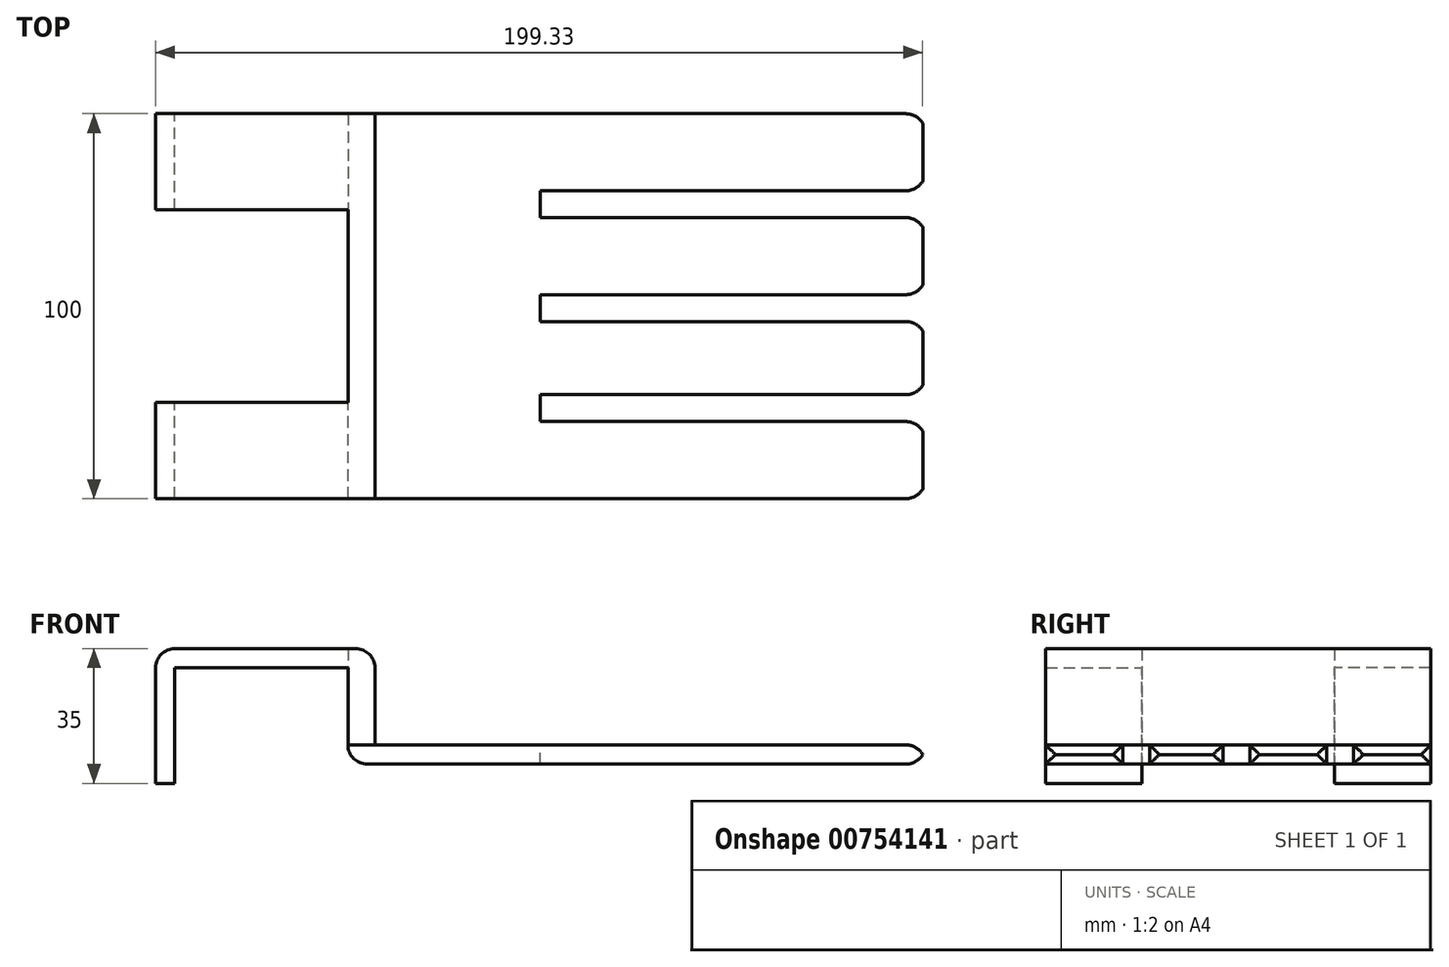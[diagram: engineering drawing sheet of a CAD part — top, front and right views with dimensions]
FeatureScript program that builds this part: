
annotation { "Feature Type Name" : "Feature", "Feature Type Description" : "" }
export const myFeature = defineFeature(function(context is Context, id is Id, definition is map)
    precondition{}
    {
        {
            var Q0;
            Q0=qCreatedBy(makeId("Top.planeOp"),FACE);
            var sketch = newSketch(context, id + "F0", { "sketchPlane" : qUnion([Q0])});
            skLineSegment(sketch, "E0.bottom", {"start": v(-77.43, 52.19) * mm, "end": v(72.57, 52.19) * mm});
            skLineSegment(sketch, "E0.top", {"start": v(-77.43, -47.81) * mm, "end": v(72.57, -47.81) * mm});
            skLineSegment(sketch, "E0.left", {"start": v(-77.43, 52.19) * mm, "end": v(-77.43, -47.81) * mm});
            skLineSegment(sketch, "E0.right", {"start": v(72.57, 52.19) * mm, "end": v(72.57, -47.81) * mm});
            skSolve(sketch);
        }
        {
            var Q0;
            Q0=makeQuery(id+"F0.imprint","IMPRINT",FACE,{"disambiguationData":[TD([[makeQuery(id+"F0.imprint","IMPRINT",EDGE,{"derivedFrom":sQuery(id+"F0.wireOp",EDGE,"E0.bottom")}),-1.0]])]});
            extrude(context, id + "F1", {"entities" : qUnion([Q0]), "depth" : 5 * mm, "offsetDistance" : 25 * mm});
        }
        {
            var Q0;
            Q0=makeQuery(id+"F1.opExtrude","CAP_FACE",FACE,{"disambiguationData":[OSD([sQuery(id+"F0.wireOp",EDGE,"E0.bottom"),sQuery(id+"F0.wireOp",EDGE,"E0.top"),sQuery(id+"F0.wireOp",EDGE,"E0.left"),sQuery(id+"F0.wireOp",EDGE,"E0.right")])],"isStart":false});
            var sketch = newSketch(context, id + "F2", { "sketchPlane" : qUnion([Q0])});
            skLineSegment(sketch, "E1", {"start": v(-27.43, 52.19) * mm, "end": v(-27.43, -47.81) * mm, "construction": true});
            skLineSegment(sketch, "E2.bottom", {"start": v(-27.43, 32.19) * mm, "end": v(72.57, 32.19) * mm});
            skLineSegment(sketch, "E2.top", {"start": v(-27.43, 25.19) * mm, "end": v(72.57, 25.19) * mm});
            skLineSegment(sketch, "E2.left", {"start": v(-27.43, 32.19) * mm, "end": v(-27.43, 25.19) * mm});
            skLineSegment(sketch, "E2.right", {"start": v(72.57, 32.19) * mm, "end": v(72.57, 25.19) * mm});
            skLineSegment(sketch, "E3.bottom", {"start": v(-27.43, -20.81) * mm, "end": v(72.57, -20.81) * mm});
            skLineSegment(sketch, "E3.top", {"start": v(-27.43, -27.81) * mm, "end": v(72.57, -27.81) * mm});
            skLineSegment(sketch, "E3.left", {"start": v(-27.43, -20.81) * mm, "end": v(-27.43, -27.81) * mm});
            skLineSegment(sketch, "E3.right", {"start": v(72.57, -20.81) * mm, "end": v(72.57, -27.81) * mm});
            skLineSegment(sketch, "E4.bottom", {"start": v(-27.43, 5.19) * mm, "end": v(72.57, 5.19) * mm});
            skLineSegment(sketch, "E4.top", {"start": v(-27.43, -1.81) * mm, "end": v(72.57, -1.81) * mm});
            skLineSegment(sketch, "E4.left", {"start": v(-27.43, 5.19) * mm, "end": v(-27.43, -1.81) * mm});
            skLineSegment(sketch, "E4.right", {"start": v(72.57, 5.19) * mm, "end": v(72.57, -1.81) * mm});
            skSolve(sketch);
        }
        {
            var Q0;
            Q0=makeQuery(id+"F2.imprint","IMPRINT",FACE,{"disambiguationData":[TD([[makeQuery(id+"F2.imprint","IMPRINT",EDGE,{"derivedFrom":sQuery(id+"F2.wireOp",EDGE,"E2.bottom")}),-1.0]])]});
            var Q1;
            Q1=makeQuery(id+"F2.imprint","IMPRINT",FACE,{"disambiguationData":[TD([[makeQuery(id+"F2.imprint","IMPRINT",EDGE,{"derivedFrom":sQuery(id+"F2.wireOp",EDGE,"E4.bottom")}),-1.0]])]});
            var Q2;
            Q2=makeQuery(id+"F2.imprint","IMPRINT",FACE,{"disambiguationData":[TD([[makeQuery(id+"F2.imprint","IMPRINT",EDGE,{"derivedFrom":sQuery(id+"F2.wireOp",EDGE,"E3.bottom")}),-1.0]])]});
            extrude(context, id + "F3", {"entities" : qUnion([Q0, Q1, Q2]), "operationType" : NewBodyOperationType.REMOVE, "endBound" : BoundingType.THROUGH_ALL, "oppositeDirection" : true, "depth" : 25 * mm, "offsetDistance" : 25 * mm});
        }
        {
            var Q0;
            Q0=makeQuery(id+"F1.opExtrude","CAP_FACE",FACE,{"disambiguationData":[OSD([sQuery(id+"F0.wireOp",EDGE,"E0.bottom"),sQuery(id+"F0.wireOp",EDGE,"E0.top"),sQuery(id+"F0.wireOp",EDGE,"E0.left"),sQuery(id+"F0.wireOp",EDGE,"E0.right")])],"isStart":false});
            var sketch = newSketch(context, id + "F4", { "sketchPlane" : qUnion([Q0])});
            skLineSegment(sketch, "E5.bottom", {"start": v(-77.43, 52.19) * mm, "end": v(-70.43, 52.19) * mm});
            skLineSegment(sketch, "E5.top", {"start": v(-77.43, -47.81) * mm, "end": v(-70.43, -47.81) * mm});
            skLineSegment(sketch, "E5.left", {"start": v(-77.43, 52.19) * mm, "end": v(-77.43, -47.81) * mm});
            skLineSegment(sketch, "E5.right", {"start": v(-70.43, 52.19) * mm, "end": v(-70.43, -47.81) * mm});
            skSolve(sketch);
        }
        {
            var Q0;
            Q0=makeQuery(id+"F4.imprint","IMPRINT",FACE,{"disambiguationData":[TD([[makeQuery(id+"F4.imprint","IMPRINT",EDGE,{"derivedFrom":sQuery(id+"F4.wireOp",EDGE,"E5.bottom")}),-1.0]])]});
            extrude(context, id + "F5", {"entities" : qUnion([Q0]), "depth" : 25 * mm, "offsetDistance" : 25 * mm});
        }
        {
            var Q0;
            Q0=makeQuery(id+"F5.opExtrude","SWEPT_FACE",FACE,{"disambiguationData":[OSD([sQuery(id+"F4.wireOp",EDGE,"E5.left")])]});
            var sketch = newSketch(context, id + "F6", { "sketchPlane" : qUnion([Q0])});
            skLineSegment(sketch, "E6.bottom", {"start": v(-52.19, 30) * mm, "end": v(-27.19, 30) * mm});
            skLineSegment(sketch, "E6.top", {"start": v(-52.19, 25) * mm, "end": v(-27.19, 25) * mm});
            skLineSegment(sketch, "E6.left", {"start": v(-52.19, 30) * mm, "end": v(-52.19, 25) * mm});
            skLineSegment(sketch, "E6.right", {"start": v(-27.19, 30) * mm, "end": v(-27.19, 25) * mm});
            skLineSegment(sketch, "E7.bottom", {"start": v(47.81, 30) * mm, "end": v(22.81, 30) * mm});
            skLineSegment(sketch, "E7.top", {"start": v(47.81, 25) * mm, "end": v(22.81, 25) * mm});
            skLineSegment(sketch, "E7.left", {"start": v(47.81, 30) * mm, "end": v(47.81, 25) * mm});
            skLineSegment(sketch, "E7.right", {"start": v(22.81, 30) * mm, "end": v(22.81, 25) * mm});
            skSolve(sketch);
        }
        {
            var Q0;
            Q0=makeQuery(id+"F6.imprint","IMPRINT",FACE,{"disambiguationData":[TD([[makeQuery(id+"F6.imprint","IMPRINT",EDGE,{"derivedFrom":sQuery(id+"F6.wireOp",EDGE,"E6.bottom")}),-1.0]])]});
            var Q1;
            Q1=makeQuery(id+"F6.imprint","IMPRINT",FACE,{"disambiguationData":[TD([[makeQuery(id+"F6.imprint","IMPRINT",EDGE,{"derivedFrom":sQuery(id+"F6.wireOp",EDGE,"E7.bottom")}),-1.0]])]});
            extrude(context, id + "F7", {"entities" : qUnion([Q0, Q1]), "operationType" : NewBodyOperationType.ADD, "depth" : 50 * mm, "offsetDistance" : 25 * mm});
        }
        {
            var Q0;
            Q0=makeQuery(id+"F7.opExtrude","SWEPT_FACE",FACE,{"disambiguationData":[OSD([sQuery(id+"F6.wireOp",EDGE,"E6.top")])]});
            var sketch = newSketch(context, id + "F8", { "sketchPlane" : qUnion([Q0])});
            skLineSegment(sketch, "E8.bottom", {"start": v(-127.43, -27.19) * mm, "end": v(-122.43, -27.19) * mm});
            skLineSegment(sketch, "E8.top", {"start": v(-127.43, -52.19) * mm, "end": v(-122.43, -52.19) * mm});
            skLineSegment(sketch, "E8.left", {"start": v(-127.43, -27.19) * mm, "end": v(-127.43, -52.19) * mm});
            skLineSegment(sketch, "E8.right", {"start": v(-122.43, -27.19) * mm, "end": v(-122.43, -52.19) * mm});
            skSolve(sketch);
        }
        {
            var Q0;
            Q0=makeQuery(id+"F7.opExtrude","SWEPT_FACE",FACE,{"disambiguationData":[OSD([sQuery(id+"F6.wireOp",EDGE,"E7.top")])]});
            var sketch = newSketch(context, id + "F9", { "sketchPlane" : qUnion([Q0])});
            skLineSegment(sketch, "E9.bottom", {"start": v(-127.43, 47.81) * mm, "end": v(-122.43, 47.81) * mm});
            skLineSegment(sketch, "E9.top", {"start": v(-127.43, 22.81) * mm, "end": v(-122.43, 22.81) * mm});
            skLineSegment(sketch, "E9.left", {"start": v(-127.43, 47.81) * mm, "end": v(-127.43, 22.81) * mm});
            skLineSegment(sketch, "E9.right", {"start": v(-122.43, 47.81) * mm, "end": v(-122.43, 22.81) * mm});
            skSolve(sketch);
        }
        {
            var Q0;
            Q0=makeQuery(id+"F9.imprint","IMPRINT",FACE,{"disambiguationData":[TD([[makeQuery(id+"F9.imprint","IMPRINT",EDGE,{"derivedFrom":sQuery(id+"F9.wireOp",EDGE,"E9.bottom")}),-1.0]])]});
            var Q1;
            Q1=makeQuery(id+"F8.imprint","IMPRINT",FACE,{"disambiguationData":[TD([[makeQuery(id+"F8.imprint","IMPRINT",EDGE,{"derivedFrom":sQuery(id+"F8.wireOp",EDGE,"E8.bottom")}),-1.0]])]});
            extrude(context, id + "F10", {"entities" : qUnion([Q0, Q1]), "operationType" : NewBodyOperationType.ADD, "depth" : 30 * mm, "offsetDistance" : 25 * mm});
        }
        {
            var Q0;
            Q0=makeQuery(id+"F7.opExtrude","CAP_EDGE",EDGE,{"disambiguationData":[OSD([sQuery(id+"F6.wireOp",EDGE,"E6.bottom")])],"isStart":false});
            var Q1;
            Q1=makeQuery(id+"F7.opExtrude","CAP_EDGE",EDGE,{"disambiguationData":[OSD([sQuery(id+"F6.wireOp",EDGE,"E7.bottom")])],"isStart":false});
            var Q2;
            Q2=makeQuery(id+"F5.opExtrude","CAP_EDGE",EDGE,{"disambiguationData":[OSD([sQuery(id+"F4.wireOp",EDGE,"E5.right")])],"isStart":false});
            var Q3;
            Q3=makeQuery(id+"F1.opExtrude","CAP_EDGE",EDGE,{"disambiguationData":[OSD([sQuery(id+"F0.wireOp",EDGE,"E0.left")])],"isStart":true});
            fillet(context, id + "F11", {"entities" : qUnion([Q0, Q1, Q2, Q3]), "radius" : 5 * mm, "tangentPropagation" : true, "allowEdgeOverflow" : false});
        }
        {
            var Q0;
            {var subQ0=sQuery(id+"F0.wireOp",EDGE,"E0.right");var subQ2=sQuery(id+"F0.wireOp",EDGE,"E0.top");Q0=makeQuery(id+"F3.boolean.opBoolean","SPLIT",FACE,{"disambiguationData":[TD([makeQuery(id+"F1.opExtrude","SWEPT_FACE",FACE,{"disambiguationData":[OSD([subQ2])]})])],"derivedFrom":makeQuery(id+"F1.opExtrude","SWEPT_FACE",FACE,{"disambiguationData":[OSD([subQ0])]})});}
            var Q1;
            {var subQ0=sQuery(id+"F0.wireOp",EDGE,"E0.right");Q1=makeQuery(id+"F3.boolean.opBoolean","SPLIT",FACE,{"disambiguationData":[TD([makeQuery(id+"F3.opExtrude","SWEPT_FACE",FACE,{"disambiguationData":[OSD([sQuery(id+"F2.wireOp",EDGE,"E3.bottom")])]})])],"derivedFrom":makeQuery(id+"F1.opExtrude","SWEPT_FACE",FACE,{"disambiguationData":[OSD([subQ0])]})});}
            var Q2;
            {var subQ0=sQuery(id+"F0.wireOp",EDGE,"E0.right");Q2=makeQuery(id+"F3.boolean.opBoolean","SPLIT",FACE,{"disambiguationData":[TD([makeQuery(id+"F3.opExtrude","SWEPT_FACE",FACE,{"disambiguationData":[OSD([sQuery(id+"F2.wireOp",EDGE,"E2.top")])]})])],"derivedFrom":makeQuery(id+"F1.opExtrude","SWEPT_FACE",FACE,{"disambiguationData":[OSD([subQ0])]})});}
            var Q3;
            {var subQ0=sQuery(id+"F0.wireOp",EDGE,"E0.bottom");var subQ1=sQuery(id+"F0.wireOp",EDGE,"E0.right");Q3=makeQuery(id+"F3.boolean.opBoolean","SPLIT",FACE,{"disambiguationData":[TD([makeQuery(id+"F1.opExtrude","SWEPT_FACE",FACE,{"disambiguationData":[OSD([subQ0])]})])],"derivedFrom":makeQuery(id+"F1.opExtrude","SWEPT_FACE",FACE,{"disambiguationData":[OSD([subQ1])]})});}
            fillet(context, id + "F12", {"entities" : qUnion([Q0, Q1, Q2, Q3]), "radius" : 5 * mm, "tangentPropagation" : true, "allowEdgeOverflow" : false});
        }
    });
